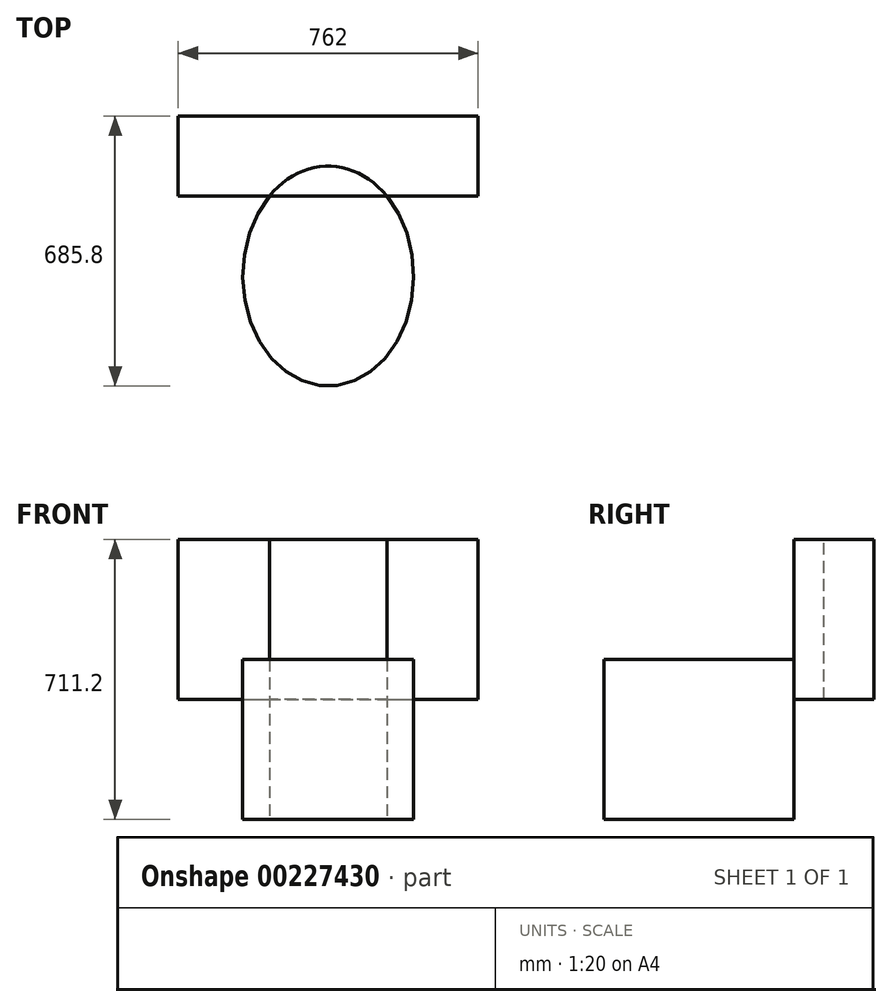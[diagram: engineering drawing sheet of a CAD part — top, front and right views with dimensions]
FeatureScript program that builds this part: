
annotation { "Feature Type Name" : "Feature", "Feature Type Description" : "" }
export const myFeature = defineFeature(function(context is Context, id is Id, definition is map)
    precondition{}
    {
        {
            var Q0;
            Q0=qCreatedBy(makeId("Top.planeOp"),FACE);
            var sketch = newSketch(context, id + "F0", { "sketchPlane" : qUnion([Q0])});
            skLineSegment(sketch, "E0.bottom", {"start": v(-383.9, 0) * mm, "end": v(378.1, 0) * mm});
            skLineSegment(sketch, "E0.top", {"start": v(-383.9, -203.2) * mm, "end": v(378.1, -203.2) * mm});
            skLineSegment(sketch, "E0.left", {"start": v(-383.9, 0) * mm, "end": v(-383.9, -203.2) * mm});
            skLineSegment(sketch, "E0.right", {"start": v(378.1, 0) * mm, "end": v(378.1, -203.2) * mm});
            skLineSegment(sketch, "E1.bottom", {"start": v(-286.61, -203.2) * mm, "end": v(19.42, -203.2) * mm});
            skEllipse(sketch, "E2", {"center": v(-2.9, -406.4) * mm, "majorRadius": 279.4 * mm, "minorRadius": 216.92 * mm, "majorAxis": v(0, 1)});
            skPoint(sketch, "E3", {"position": v(-2.9, 0) * mm});
            skSolve(sketch);
        }
        {
            var Q0;
            {var subQ0=sQuery(id+"F0.wireOp",EDGE,"E1.top");Q0=makeQuery(id+"F0.imprint","IMPRINT",FACE,{"disambiguationData":[TD([[makeQuery(id+"F0.imprint","IMPRINT",EDGE,{"derivedFrom":subQ0}),-1.0]])]});}
            var Q1;
            {var subQ1=sQuery(id+"F0.wireOp",EDGE,"E1.top");Q1=makeQuery(id+"F0.imprint","IMPRINT",FACE,{"disambiguationData":[TD([[makeQuery(id+"F0.imprint","IMPRINT",EDGE,{"derivedFrom":subQ1}),1.0]])]});}
            var Q2;
            {var subQ0=sQuery(id+"F0.wireOp",EDGE,"E2");var subQ1=sQuery(id+"F0.wireOp",EDGE,"E1.bottom");var subQ2=makeQuery(id+"F0.imprint","INTERSECT",VERTEX,{"disambiguationData":[OD(0.0)],"derivedFrom":[subQ1,subQ0]});Q2=makeQuery(id+"F0.imprint","IMPRINT",FACE,{"disambiguationData":[TD([[makeQuery(id+"F0.imprint","IMPRINT",EDGE,{"disambiguationData":[TD([[subQ2,-1.0]])],"derivedFrom":subQ1}),1.0]])]});}
            var Q3;
            {var subQ0=sQuery(id+"F0.wireOp",EDGE,"E1.bottom");var subQ1=sQuery(id+"F0.wireOp",EDGE,"E0.top");var subQ2=makeQuery(id+"F0.imprint","INTERSECT",VERTEX,{"disambiguationData":[OD(1.0)],"derivedFrom":[subQ1,subQ0]});Q3=makeQuery(id+"F0.imprint","IMPRINT",FACE,{"disambiguationData":[TD([[makeQuery(id+"F0.imprint","IMPRINT",EDGE,{"disambiguationData":[TD([[subQ2,-1.0]])],"derivedFrom":subQ1}),-1.0]])]});}
            extrude(context, id + "F1", {"entities" : qUnion([Q0, Q1, Q2, Q3]), "depth" : 406.4 * mm});
        }
        {
            var Q0;
            Q0=makeQuery(id+"F0.imprint","IMPRINT",FACE,{"disambiguationData":[TD([[makeQuery(id+"F0.imprint","IMPRINT",EDGE,{"derivedFrom":sQuery(id+"F0.wireOp",EDGE,"E0.bottom")}),-1.0]])]});
            var Q1;
            {var subQ0=sQuery(id+"F0.wireOp",EDGE,"E2");var subQ1=sQuery(id+"F0.wireOp",EDGE,"E1.bottom");var subQ2=makeQuery(id+"F0.imprint","INTERSECT",VERTEX,{"disambiguationData":[OD(0.0)],"derivedFrom":[subQ1,subQ0]});Q1=makeQuery(id+"F0.imprint","IMPRINT",FACE,{"disambiguationData":[TD([[makeQuery(id+"F0.imprint","IMPRINT",EDGE,{"disambiguationData":[TD([[subQ2,-1.0]])],"derivedFrom":subQ1}),1.0]])]});}
            extrude(context, id + "F2", {"entities" : qUnion([Q0, Q1]), "operationType" : NewBodyOperationType.ADD, "depth" : 711.2 * mm, "hasSecondDirection" : true, "secondDirectionOppositeDirection" : false, "secondDirectionDepth" : 304.8 * mm});
        }
    });
